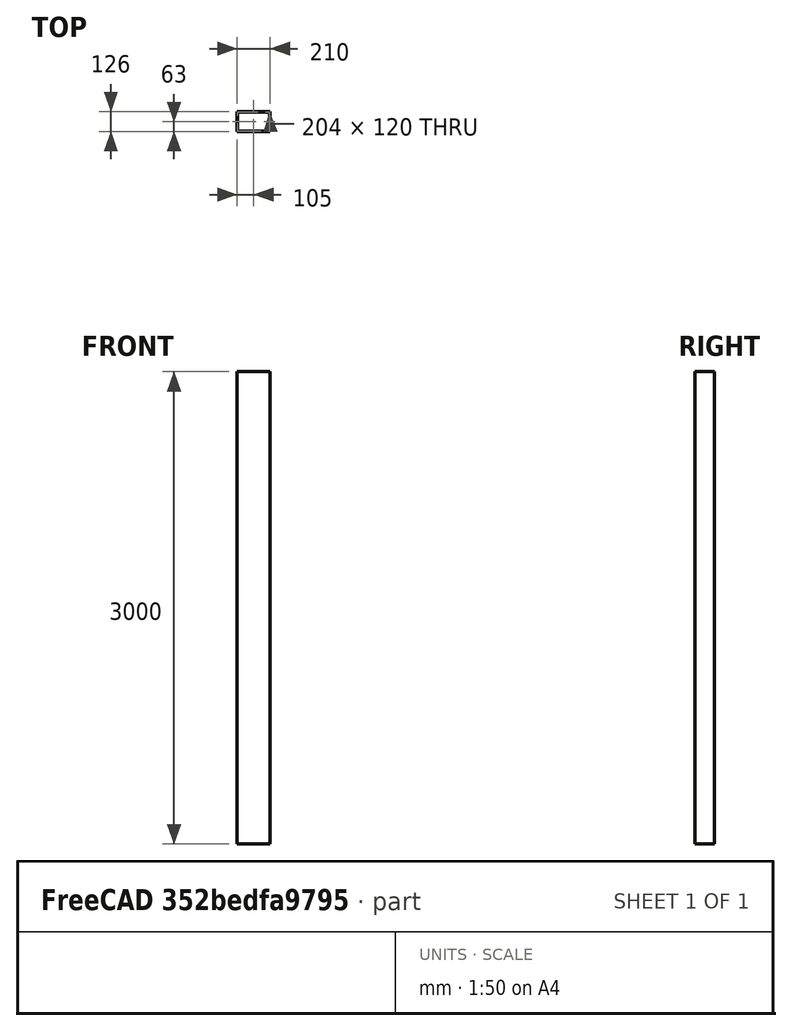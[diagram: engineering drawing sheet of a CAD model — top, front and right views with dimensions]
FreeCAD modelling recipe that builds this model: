
FCSTD DOCUMENT  (FreeCAD 0.21R33771 (Git))
Label: PQ4_beampipe
License: All rights reserved
LicenseURL: https://en.wikipedia.org/wiki/All_rights_reserved
objects: Sketcher::SketchObject×1, PartDesign::Pad×1, PartDesign::Body×1
note: 4 computed .brp shape members not serialized (recipe doc carries the construction recipe); baked Part::Feature solids carry a one-line shape summary decoded from their .brp

FEATURE [Sketcher::SketchObject] Sketch
  FullyConstrained = true
  MapMode = 5
  Support = -> [XY_Plane]
  sketch-geometry (10):
    g0: LineSegment StartX=-102 StartY=-60 StartZ=0 EndX=-102 EndY=60 EndZ=0
    g1: LineSegment StartX=-102 StartY=60 StartZ=0 EndX=102 EndY=60 EndZ=0
    g2: LineSegment StartX=102 StartY=60 StartZ=0 EndX=102 EndY=-60 EndZ=0
    g3: LineSegment StartX=102 StartY=-60 StartZ=0 EndX=-102 EndY=-60 EndZ=0
    g4: GeomPoint X=0 Y=0 Z=0
    g5: LineSegment StartX=-105 StartY=-63 StartZ=0 EndX=-105 EndY=63 EndZ=0
    g6: LineSegment StartX=-105 StartY=63 StartZ=0 EndX=105 EndY=63 EndZ=0
    g7: LineSegment StartX=105 StartY=63 StartZ=0 EndX=105 EndY=-63 EndZ=0
    g8: LineSegment StartX=105 StartY=-63 StartZ=0 EndX=-105 EndY=-63 EndZ=0
    g9: GeomPoint X=0 Y=0 Z=0
  constraints (24):
    c: Coincident(g0,g1)
    c: Coincident(g1,g2)
    c: Coincident(g2,g3)
    c: Coincident(g3,g0)
    c: Horizontal(g1)
    c: Horizontal(g3)
    c: Vertical(g0)
    c: Vertical(g2)
    c: Symmetric(g1,g0,g4)
    c: Coincident(g4,g-1)
    c: Coincident(g5,g6)
    c: Coincident(g6,g7)
    c: Coincident(g7,g8)
    c: Coincident(g8,g5)
    c: Horizontal(g6)
    c: Horizontal(g8)
    c: Vertical(g5)
    c: Vertical(g7)
    c: Symmetric(g6,g5,g9)
    c: Coincident(g9,g4)
    c: DistanceX(g1,g1) = 204
    c: DistanceX(g6,g6) = 210
    c: DistanceY(g2,g2) = 120
    c: DistanceY(g7,g7) = 126
FEATURE [PartDesign::Pad] Pad
  Direction = (0,0,1)
  Length = 3000
  Length2 = 10
  Midplane = true
  Profile = -> Sketch
  ReferenceAxis = -> Sketch [N_Axis]
  Type = 0
FEATURE [PartDesign::Body] Body
  Group = -> [Sketch,Pad]
  Origin = -> Origin
  Tip = -> Pad
